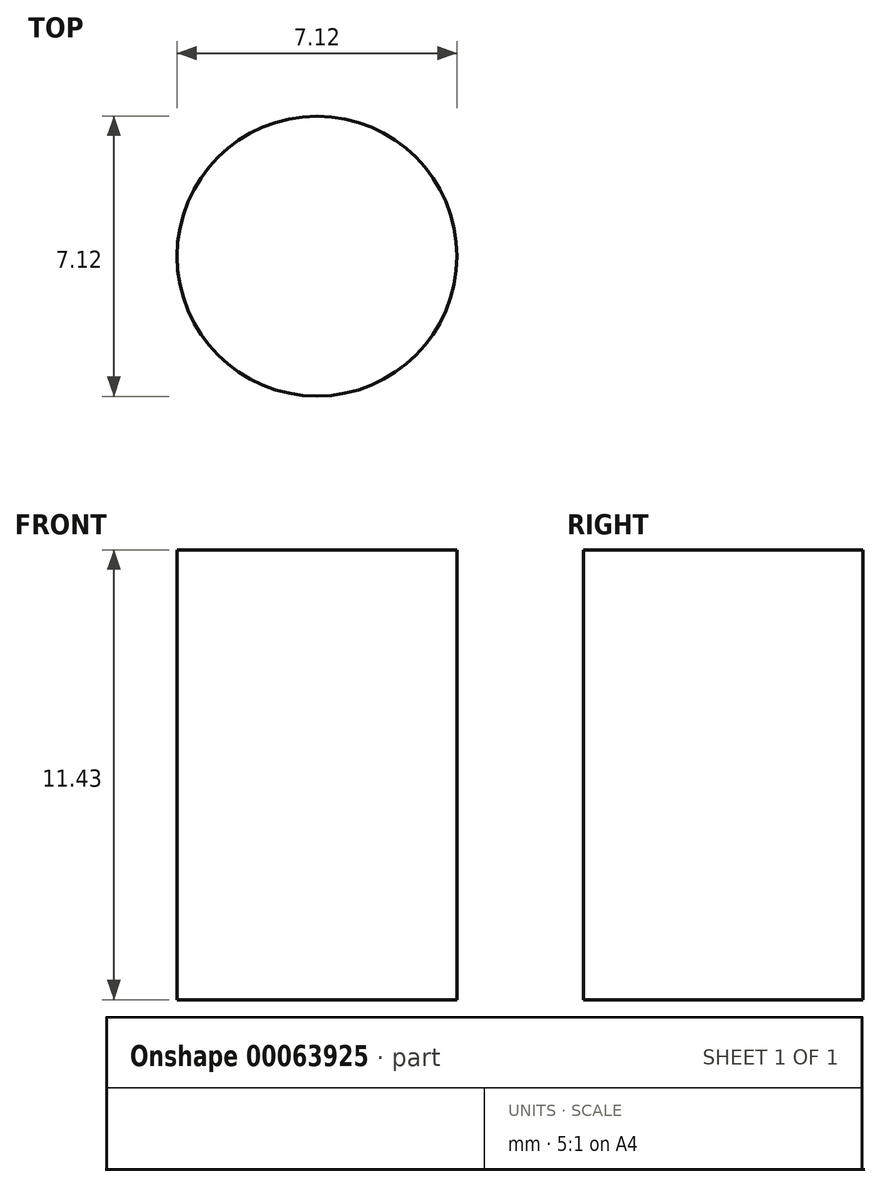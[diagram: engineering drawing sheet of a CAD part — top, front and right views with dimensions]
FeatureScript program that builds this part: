
annotation { "Feature Type Name" : "Feature", "Feature Type Description" : "" }
export const myFeature = defineFeature(function(context is Context, id is Id, definition is map)
    precondition{}
    {
        {
            var Q0;
            Q0=qCreatedBy(makeId("Top.planeOp"),FACE);
            var sketch = newSketch(context, id + "F0", { "sketchPlane" : qUnion([Q0])});
            skCircle(sketch, "E0", {"center": v(0, 0) * mm, "radius": 3.56 * mm});
            skSolve(sketch);
        }
        {
            var Q0;
            Q0 = qSketchRegion(id + "F0", true);
            extrude(context, id + "F1", {"entities" : qUnion([Q0]), "depth" : 11.43 * mm});
        }
    });
